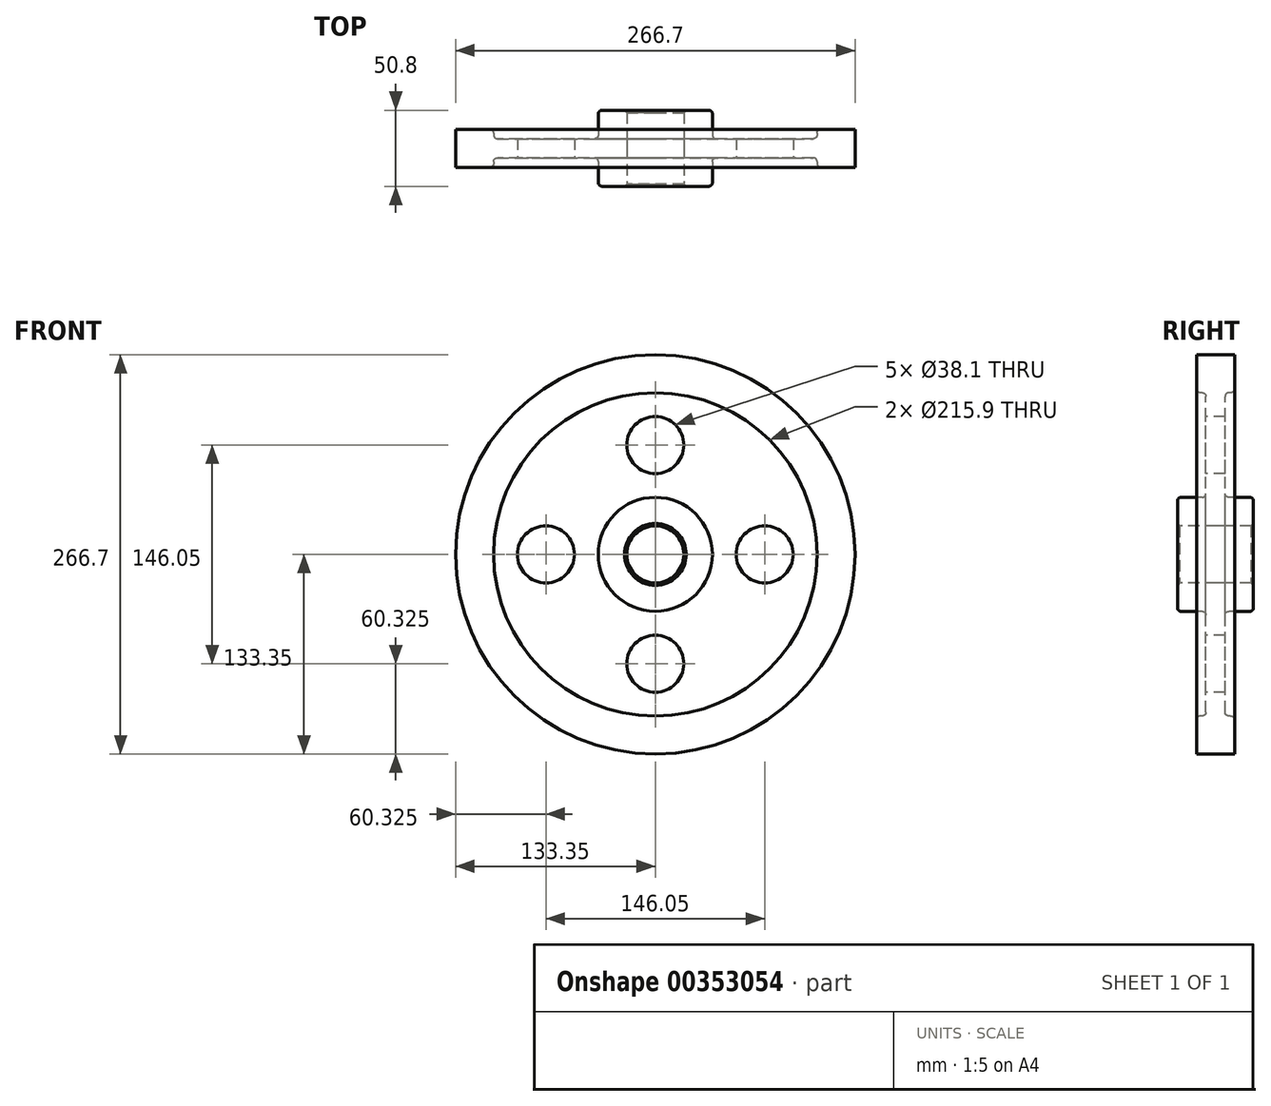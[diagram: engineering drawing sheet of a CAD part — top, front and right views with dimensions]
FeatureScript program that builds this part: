
annotation { "Feature Type Name" : "Feature", "Feature Type Description" : "" }
export const myFeature = defineFeature(function(context is Context, id is Id, definition is map)
    precondition{}
    {
        {
            var Q0;
            Q0=qCreatedBy(makeId("Right.planeOp"),FACE);
            var sketch = newSketch(context, id + "F0", { "sketchPlane" : qUnion([Q0])});
            skLineSegment(sketch, "E0", {"start": v(0, 0) * mm, "end": v(76.05, 0) * mm, "construction": true});
            skLineSegment(sketch, "E1.0", {"start": v(6.35, 38.1) * mm, "end": v(25.4, 38.1) * mm});
            skLineSegment(sketch, "E2.0", {"start": v(6.35, 107.95) * mm, "end": v(12.7, 107.95) * mm});
            skLineSegment(sketch, "E3", {"start": v(0, 0) * mm, "end": v(0, 133.35) * mm, "construction": true});
            skLineSegment(sketch, "E4.1", {"start": v(6.35, 38.1) * mm, "end": v(6.35, 107.95) * mm});
            skLineSegment(sketch, "E5", {"start": v(0, 133.35) * mm, "end": v(12.7, 133.35) * mm});
            skLineSegment(sketch, "E6", {"start": v(12.7, 133.35) * mm, "end": v(12.7, 107.95) * mm});
            skLineSegment(sketch, "E7", {"start": v(25.4, 38.1) * mm, "end": v(25.4, 19.05) * mm});
            skLineSegment(sketch, "E8.MirrorCS", {"start": v(-6.35, 38.1) * mm, "end": v(-6.35, 107.95) * mm});
            skLineSegment(sketch, "E9.MirrorCS", {"start": v(-6.35, 107.95) * mm, "end": v(-12.7, 107.95) * mm});
            skLineSegment(sketch, "E10.MirrorCS", {"start": v(-12.7, 133.35) * mm, "end": v(-12.7, 107.95) * mm});
            skLineSegment(sketch, "E11.MirrorCS", {"start": v(0, 133.35) * mm, "end": v(-12.7, 133.35) * mm});
            skLineSegment(sketch, "E12.MirrorCS", {"start": v(-6.35, 38.1) * mm, "end": v(-25.4, 38.1) * mm});
            skLineSegment(sketch, "E13.MirrorCS", {"start": v(-25.4, 38.1) * mm, "end": v(-25.4, 19.05) * mm});
            skLineSegment(sketch, "E14.MirrorCS", {"start": v(0, 0) * mm, "end": v(-76.05, 0) * mm, "construction": true});
            skLineSegment(sketch, "E15", {"start": v(-25.4, 0) * mm, "end": v(25.4, 0) * mm});
            skLineSegment(sketch, "E16.0", {"start": v(25.4, 19.05) * mm, "end": v(-76.05, 19.05) * mm});
            skPoint(sketch, "E17.orphan", {"position": v(25.4, 0) * mm});
            skPoint(sketch, "E18.orphan", {"position": v(-25.4, 0) * mm});
            skSolve(sketch);
        }
        {
            var Q0;
            Q0=makeQuery(id+"F0.imprint","IMPRINT",FACE,{"disambiguationData":[TD([[makeQuery(id+"F0.imprint","IMPRINT",EDGE,{"derivedFrom":sQuery(id+"F0.wireOp",EDGE,"E2.0")}),1.0]])]});
            var Q1;
            Q1=sQuery(id+"F0.wireOp",EDGE,"E0");
            revolve(context, id + "F1", {"entities" : qUnion([Q0]), "axis" : qUnion([Q1]), "revolveType" : RevolveType.FULL});
        }
        {
            var Q0;
            Q0=makeQuery(id+"F1.opRevolve","SWEPT_FACE",FACE,{"disambiguationData":[OSD([sQuery(id+"F0.wireOp",EDGE,"E8.MirrorCS")])]});
            var sketch = newSketch(context, id + "F2", { "sketchPlane" : qUnion([Q0])});
            skLineSegment(sketch, "E19", {"start": v(0, 0) * mm, "end": v(0, 73.03) * mm});
            skCircle(sketch, "E20", {"center": v(0, 73.03) * mm, "radius": 19.05 * mm});
            skCircle(sketch, "E21.1.0", {"center": v(-73.03, 0) * mm, "radius": 19.05 * mm});
            skCircle(sketch, "E21.2.0", {"center": v(0, -73.03) * mm, "radius": 19.05 * mm});
            skCircle(sketch, "E21.3.0", {"center": v(73.03, 0) * mm, "radius": 19.05 * mm});
            skPoint(sketch, "E21.center", {"position": v(0, 0) * mm});
            skSolve(sketch);
        }
        {
            var Q0;
            Q0=makeQuery(id+"F2.imprint","IMPRINT",FACE,{"disambiguationData":[TD([[makeQuery(id+"F2.imprint","IMPRINT",EDGE,{"derivedFrom":sQuery(id+"F2.wireOp",EDGE,"E21.1.0")}),1.0]])]});
            var Q1;
            Q1=makeQuery(id+"F2.imprint","IMPRINT",FACE,{"disambiguationData":[TD([[makeQuery(id+"F2.imprint","IMPRINT",EDGE,{"derivedFrom":sQuery(id+"F2.wireOp",EDGE,"E21.2.0")}),1.0]])]});
            var Q2;
            Q2=makeQuery(id+"F2.imprint","IMPRINT",FACE,{"disambiguationData":[TD([[makeQuery(id+"F2.imprint","IMPRINT",EDGE,{"derivedFrom":sQuery(id+"F2.wireOp",EDGE,"E21.3.0")}),1.0]])]});
            var Q3;
            Q3=makeQuery(id+"F2.imprint","IMPRINT",FACE,{"disambiguationData":[TD([[makeQuery(id+"F2.imprint","IMPRINT",EDGE,{"derivedFrom":sQuery(id+"F2.wireOp",EDGE,"E20")}),1.0]])]});
            extrude(context, id + "F3", {"entities" : qUnion([Q0, Q1, Q2, Q3]), "operationType" : NewBodyOperationType.REMOVE, "oppositeDirection" : true, "depth" : 25.4 * mm});
        }
        {
            var Q0;
            Q0=makeQuery(id+"F1.opRevolve","SWEPT_EDGE",EDGE,{"disambiguationData":[OSD([sQuery(id+"F0.wireOp",EDGE,"E9.MirrorCS"),sQuery(id+"F0.wireOp",EDGE,"E8.MirrorCS")])]});
            var Q1;
            Q1=makeQuery(id+"F1.opRevolve","SWEPT_EDGE",EDGE,{"disambiguationData":[OSD([sQuery(id+"F0.wireOp",EDGE,"E13.MirrorCS"),sQuery(id+"F0.wireOp",EDGE,"E12.MirrorCS")])]});
            var Q2;
            Q2=makeQuery(id+"F1.opRevolve","SWEPT_EDGE",EDGE,{"disambiguationData":[OSD([sQuery(id+"F0.wireOp",EDGE,"E8.MirrorCS"),sQuery(id+"F0.wireOp",EDGE,"E12.MirrorCS")])]});
            var Q3;
            Q3=makeQuery(id+"F1.opRevolve","SWEPT_EDGE",EDGE,{"disambiguationData":[OSD([sQuery(id+"F0.wireOp",EDGE,"E9.MirrorCS"),sQuery(id+"F0.wireOp",EDGE,"E10.MirrorCS")])]});
            var Q4;
            Q4=makeQuery(id+"F1.opRevolve","SWEPT_EDGE",EDGE,{"disambiguationData":[OSD([sQuery(id+"F0.wireOp",EDGE,"E7"),sQuery(id+"F0.wireOp",EDGE,"E1.0")])]});
            var Q5;
            Q5=makeQuery(id+"F1.opRevolve","SWEPT_EDGE",EDGE,{"disambiguationData":[OSD([sQuery(id+"F0.wireOp",EDGE,"E2.0"),sQuery(id+"F0.wireOp",EDGE,"E4.1")])]});
            var Q6;
            Q6=makeQuery(id+"F1.opRevolve","SWEPT_EDGE",EDGE,{"disambiguationData":[OSD([sQuery(id+"F0.wireOp",EDGE,"E2.0"),sQuery(id+"F0.wireOp",EDGE,"E6")])]});
            var Q7;
            Q7=makeQuery(id+"F1.opRevolve","SWEPT_EDGE",EDGE,{"disambiguationData":[OSD([sQuery(id+"F0.wireOp",EDGE,"E4.1"),sQuery(id+"F0.wireOp",EDGE,"E1.0")])]});
            fillet(context, id + "F4", {"entities" : qUnion([Q0, Q1, Q2, Q3, Q4, Q5, Q6, Q7]), "radius" : 2.54 * mm, "tangentPropagation" : true, "allowEdgeOverflow" : false});
        }
        {
            var Q0;
            Q0=makeQuery(id+"F1.opRevolve","SWEPT_EDGE",EDGE,{"disambiguationData":[OSD([sQuery(id+"F0.wireOp",EDGE,"E13.MirrorCS"),sQuery(id+"F0.wireOp",EDGE,"E16.0")])]});
            var Q1;
            Q1=makeQuery(id+"F1.opRevolve","SWEPT_EDGE",EDGE,{"disambiguationData":[OSD([sQuery(id+"F0.wireOp",EDGE,"E7"),sQuery(id+"F0.wireOp",EDGE,"E16.0")])]});
            chamfer(context, id + "F5", {"entities" : qUnion([Q0, Q1]), "width" : 1.59 * mm, "tangentPropagation" : true});
        }
    });
